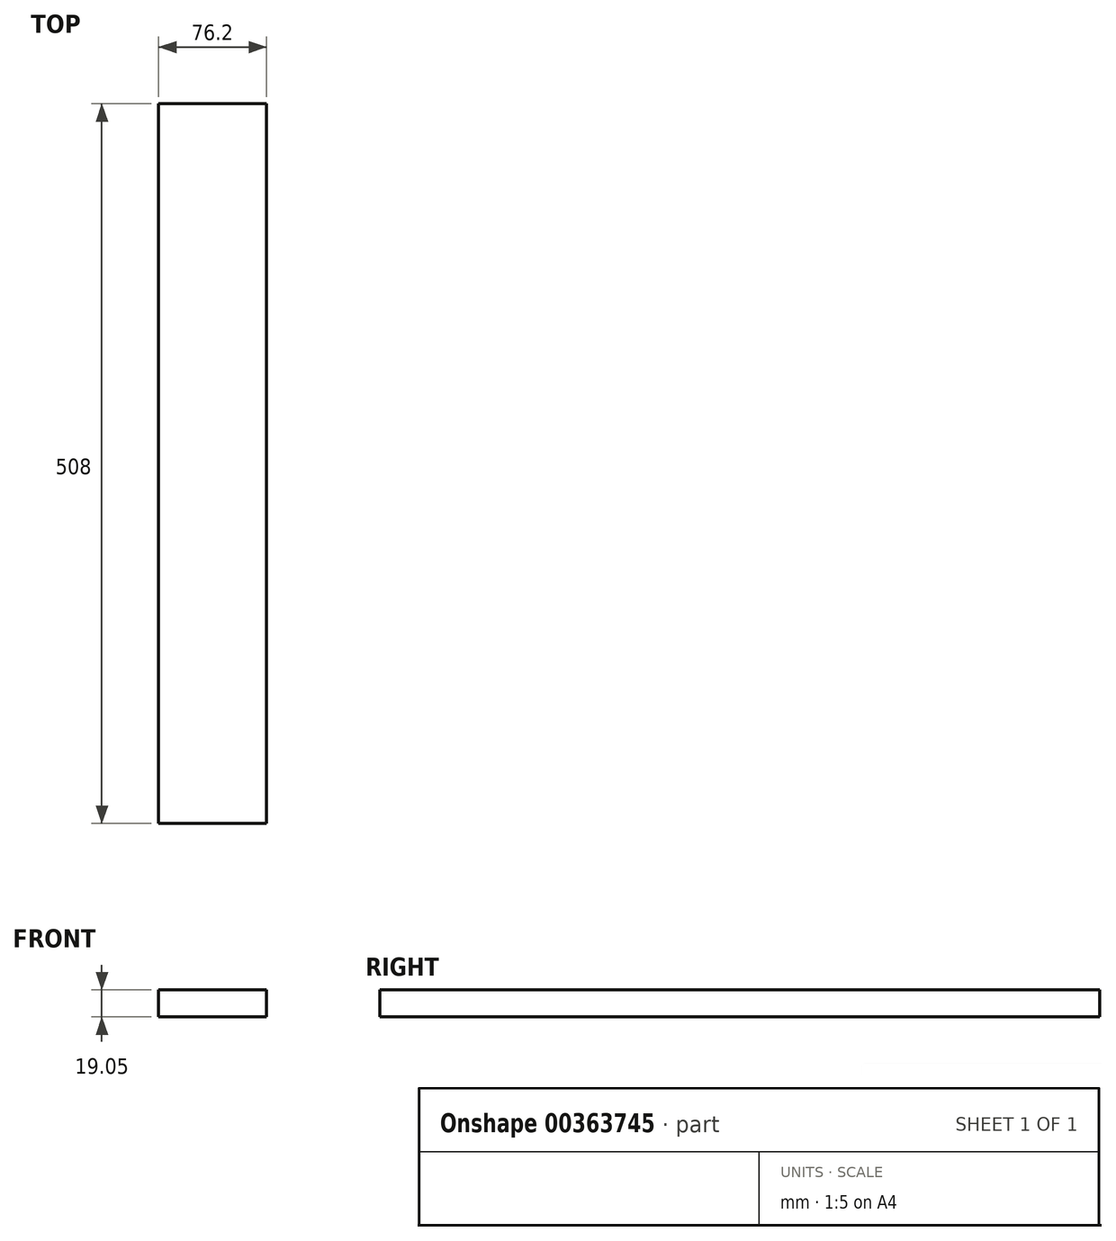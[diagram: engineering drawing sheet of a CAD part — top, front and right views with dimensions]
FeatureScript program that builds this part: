
annotation { "Feature Type Name" : "Feature", "Feature Type Description" : "" }
export const myFeature = defineFeature(function(context is Context, id is Id, definition is map)
    precondition{}
    {
        {
            var Q0;
            Q0=qCreatedBy(makeId("Top.planeOp"),FACE);
            var sketch = newSketch(context, id + "F0", { "sketchPlane" : qUnion([Q0])});
            skLineSegment(sketch, "E0.bottom", {"start": v(-38.1, 254) * mm, "end": v(38.1, 254) * mm});
            skLineSegment(sketch, "E0.top", {"start": v(-38.1, -254) * mm, "end": v(38.1, -254) * mm});
            skLineSegment(sketch, "E0.left", {"start": v(-38.1, 254) * mm, "end": v(-38.1, -254) * mm});
            skLineSegment(sketch, "E0.right", {"start": v(38.1, 254) * mm, "end": v(38.1, -254) * mm});
            skPoint(sketch, "E0.middle", {"position": v(0, 0) * mm});
            skSolve(sketch);
        }
        {
            var Q0;
            Q0 = qSketchRegion(id + "F0", true);
            extrude(context, id + "F1", {"entities" : qUnion([Q0]), "oppositeDirection" : true, "depth" : 19.05 * mm});
        }
    });
